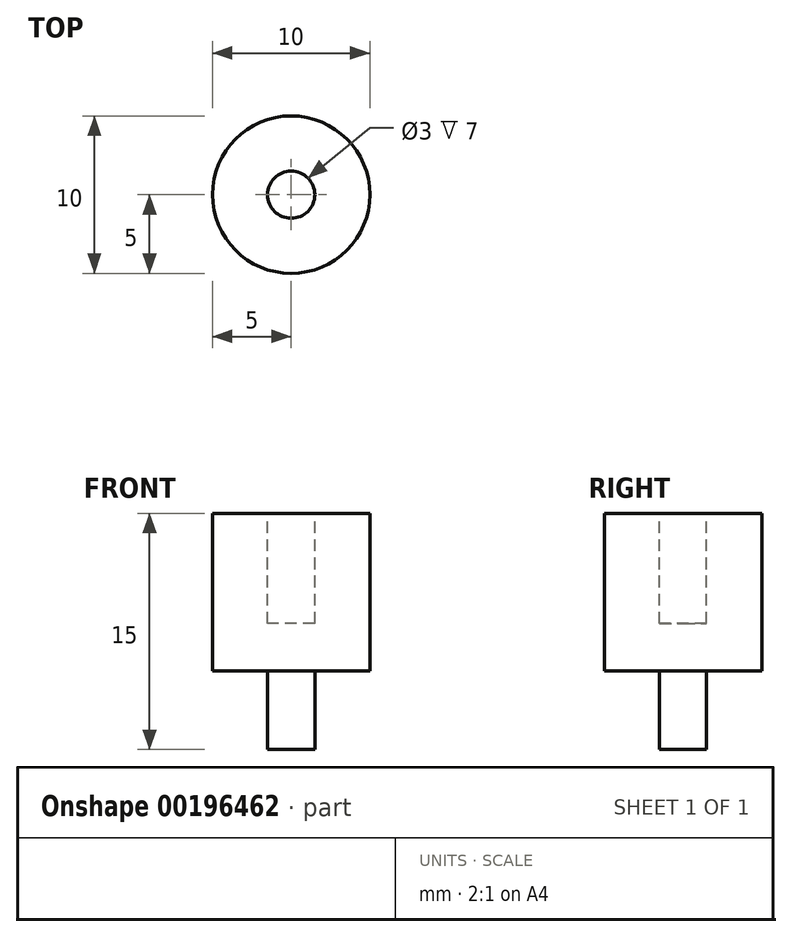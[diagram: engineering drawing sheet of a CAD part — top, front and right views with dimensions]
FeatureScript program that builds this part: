
annotation { "Feature Type Name" : "Feature", "Feature Type Description" : "" }
export const myFeature = defineFeature(function(context is Context, id is Id, definition is map)
    precondition{}
    {
        {
            var Q0;
            Q0=qCreatedBy(makeId("Top.planeOp"),FACE);
            var sketch = newSketch(context, id + "F0", { "sketchPlane" : qUnion([Q0])});
            skCircle(sketch, "E0", {"center": v(0, 0) * mm, "radius": 5 * mm});
            skSolve(sketch);
        }
        {
            var Q0;
            Q0=qSketchRegion(id+"F0",true);
            extrude(context, id + "F1", {"entities" : qUnion([Q0]), "depth" : 10 * mm});
        }
        {
            var Q0;
            Q0=makeQuery(id+"F1.opExtrude","CAP_FACE",FACE,{"disambiguationData":[OSD([sQuery(id+"F0.wireOp",EDGE,"E0")])],"isStart":false});
            var sketch = newSketch(context, id + "F2", { "sketchPlane" : qUnion([Q0])});
            skCircle(sketch, "E1", {"center": v(0, 0) * mm, "radius": 1.5 * mm});
            skSolve(sketch);
        }
        {
            var Q0;
            Q0=qSketchRegion(id+"F2",true);
            extrude(context, id + "F3", {"entities" : qUnion([Q0]), "operationType" : NewBodyOperationType.REMOVE, "oppositeDirection" : true, "depth" : 7 * mm});
        }
        {
            var Q0;
            Q0=makeQuery(id+"F1.opExtrude","CAP_FACE",FACE,{"disambiguationData":[OSD([sQuery(id+"F0.wireOp",EDGE,"E0")])],"isStart":true});
            var sketch = newSketch(context, id + "F4", { "sketchPlane" : qUnion([Q0])});
            skCircle(sketch, "E2", {"center": v(0, 0) * mm, "radius": 1.5 * mm});
            skSolve(sketch);
        }
        {
            var Q0;
            Q0=qSketchRegion(id+"F4",true);
            extrude(context, id + "F5", {"entities" : qUnion([Q0]), "operationType" : NewBodyOperationType.ADD, "depth" : 5 * mm});
        }
    });
